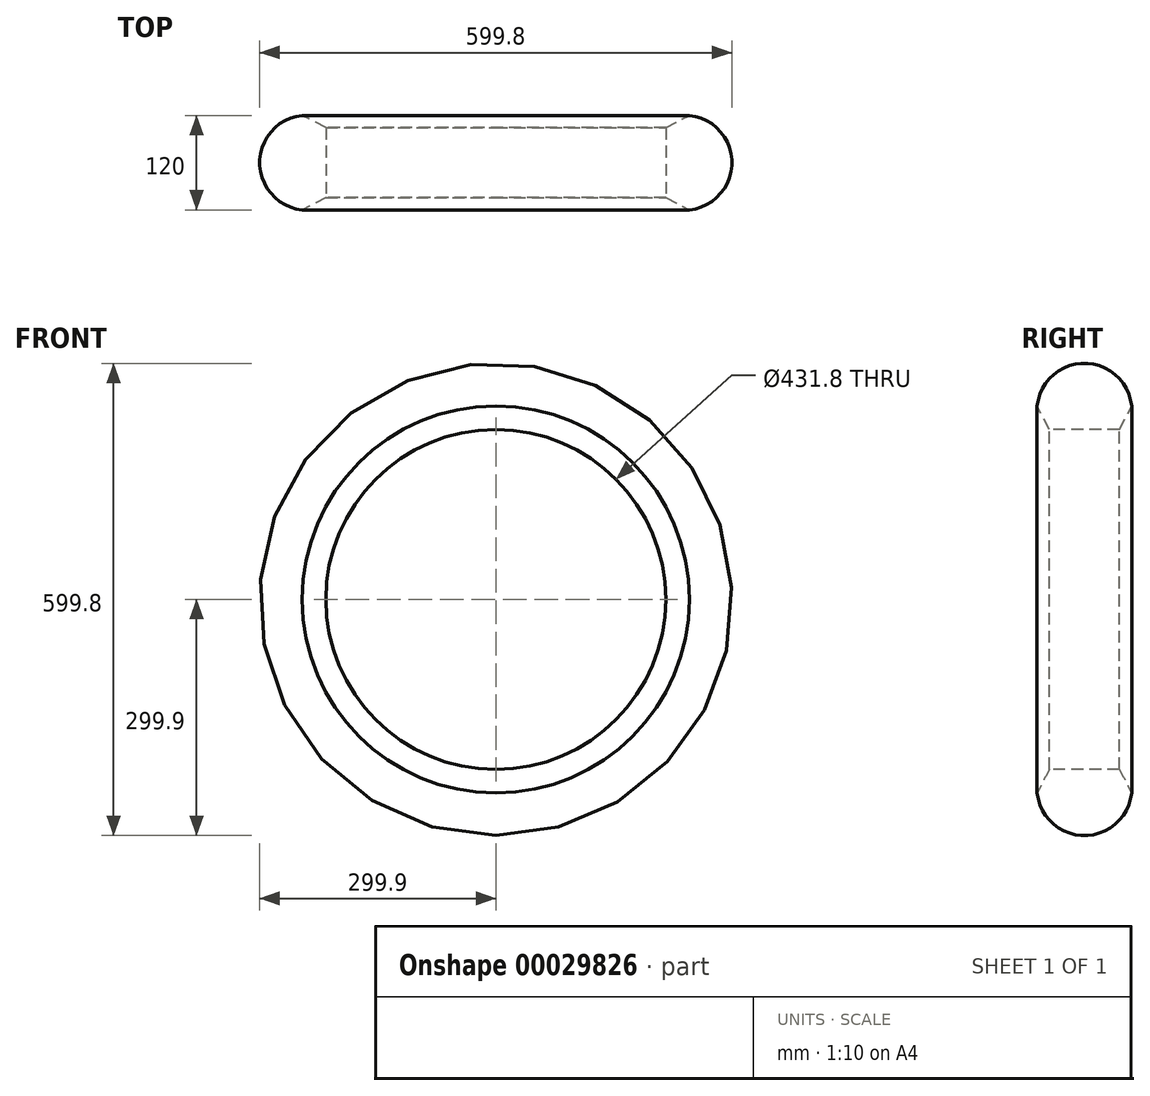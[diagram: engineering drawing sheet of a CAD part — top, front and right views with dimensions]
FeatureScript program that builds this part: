
annotation { "Feature Type Name" : "Feature", "Feature Type Description" : "" }
export const myFeature = defineFeature(function(context is Context, id is Id, definition is map)
    precondition{}
    {
        {
            var Q0;
            Q0=qCreatedBy(makeId("Right.planeOp"),FACE);
            var sketch = newSketch(context, id + "F0", { "sketchPlane" : qUnion([Q0])});
            skArc(sketch, "E0", {"start": v(60, 245.9) * mm, "mid": v(0, 299.9) * mm, "end": v(-60, 245.9) * mm});
            skLineSegment(sketch, "E1", {"start": v(-60, 245.9) * mm, "end": v(-44.45, 215.9) * mm});
            skLineSegment(sketch, "E2", {"start": v(60, 245.9) * mm, "end": v(44.45, 215.9) * mm});
            skLineSegment(sketch, "E3", {"start": v(-44.45, 215.9) * mm, "end": v(44.45, 215.9) * mm});
            skLineSegment(sketch, "E4", {"start": v(0, 0) * mm, "end": v(0, 215.9) * mm, "construction": true});
            skLineSegment(sketch, "E5", {"start": v(-55.35, 0) * mm, "end": v(56.35, 0) * mm, "construction": true});
            skSolve(sketch);
        }
        {
            var Q0;
            Q0=qSketchRegion(id+"F0",true);
            var Q1;
            Q1=sQuery(id+"F0.wireOp",EDGE,"E5");
            revolve(context, id + "F1", {"entities" : qUnion([Q0]), "axis" : qUnion([Q1]), "revolveType" : RevolveType.FULL});
        }
    });
